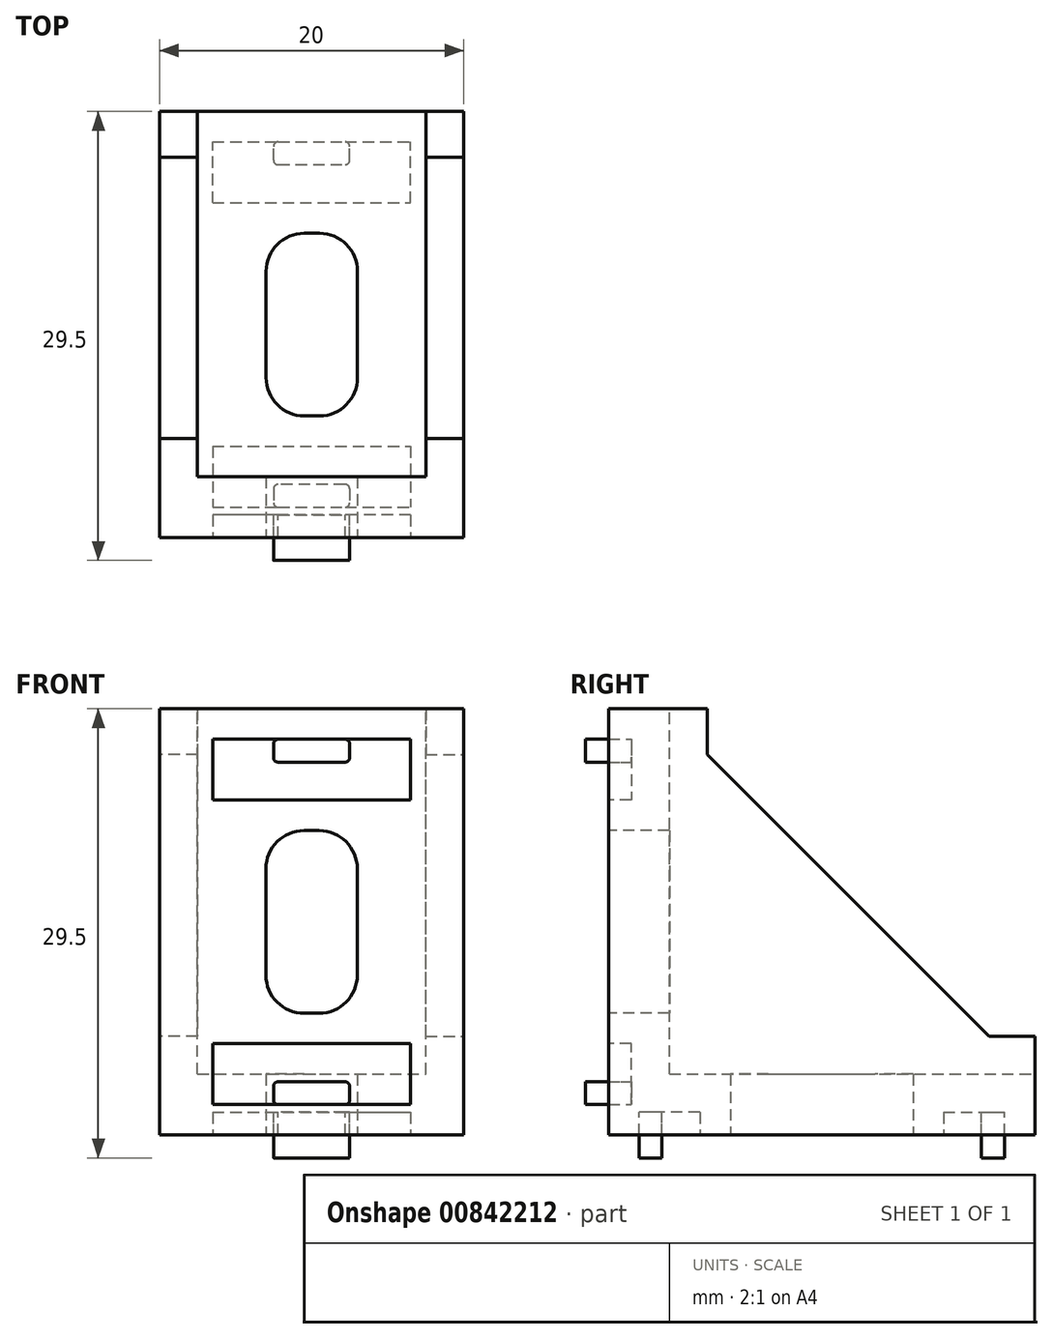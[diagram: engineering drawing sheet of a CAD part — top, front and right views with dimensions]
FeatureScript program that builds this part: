
annotation { "Feature Type Name" : "Feature", "Feature Type Description" : "" }
export const myFeature = defineFeature(function(context is Context, id is Id, definition is map)
    precondition{}
    {
        {
            var Q0;
            Q0=qCreatedBy(makeId("Top.planeOp"),FACE);
            var sketch = newSketch(context, id + "F0", { "sketchPlane" : qUnion([Q0])});
            skLineSegment(sketch, "E0.bottom", {"start": v(0, 0) * mm, "end": v(-20, 0) * mm});
            skLineSegment(sketch, "E0.top", {"start": v(0, 28) * mm, "end": v(-20, 28) * mm});
            skLineSegment(sketch, "E0.left", {"start": v(0, 0) * mm, "end": v(0, 28) * mm});
            skLineSegment(sketch, "E0.right", {"start": v(-20, 0) * mm, "end": v(-20, 28) * mm});
            skSolve(sketch);
        }
        {
            var Q0;
            Q0=makeQuery(id+"F0.imprint","IMPRINT",FACE,{"disambiguationData":[TD([[makeQuery(id+"F0.imprint","IMPRINT",EDGE,{"derivedFrom":sQuery(id+"F0.wireOp",EDGE,"E0.bottom")}),-1.0]])]});
            extrude(context, id + "F1", {"entities" : qUnion([Q0]), "depth" : 4 * mm, "offsetDistance" : 25 * mm});
        }
        {
            var Q0;
            Q0=qCreatedBy(makeId("Front.planeOp"),FACE);
            var sketch = newSketch(context, id + "F2", { "sketchPlane" : qUnion([Q0])});
            skLineSegment(sketch, "E1.bottom", {"start": v(0, 0) * mm, "end": v(-20, 0) * mm});
            skLineSegment(sketch, "E1.top", {"start": v(0, 28) * mm, "end": v(-20, 28) * mm});
            skLineSegment(sketch, "E1.left", {"start": v(0, 0) * mm, "end": v(0, 28) * mm});
            skLineSegment(sketch, "E1.right", {"start": v(-20, 0) * mm, "end": v(-20, 28) * mm});
            skSolve(sketch);
        }
        {
            var Q0;
            Q0=makeQuery(id+"F2.imprint","IMPRINT",FACE,{"disambiguationData":[TD([[makeQuery(id+"F2.imprint","IMPRINT",EDGE,{"derivedFrom":sQuery(id+"F2.wireOp",EDGE,"E1.bottom")}),-1.0]])]});
            extrude(context, id + "F3", {"entities" : qUnion([Q0]), "operationType" : NewBodyOperationType.ADD, "oppositeDirection" : true, "depth" : 4 * mm, "offsetDistance" : 25 * mm});
        }
        {
            var Q0;
            Q0=makeQuery(id+"F3.boolean.opBoolean","MERGE",FACE,{"derivedFrom":[makeQuery(id+"F1.opExtrude","SWEPT_FACE",FACE,{"disambiguationData":[OSD([sQuery(id+"F0.wireOp",EDGE,"E0.bottom")])]}),makeQuery(id+"F3.opExtrude","CAP_FACE",FACE,{"disambiguationData":[OSD([sQuery(id+"F2.wireOp",EDGE,"E1.bottom"),sQuery(id+"F2.wireOp",EDGE,"E1.top"),sQuery(id+"F2.wireOp",EDGE,"E1.left"),sQuery(id+"F2.wireOp",EDGE,"E1.right")])],"isStart":true})]});
            var sketch = newSketch(context, id + "F4", { "sketchPlane" : qUnion([Q0])});
            skLineSegment(sketch, "E2.bottom", {"start": v(-3.5, 2) * mm, "end": v(-16.5, 2) * mm});
            skLineSegment(sketch, "E2.top", {"start": v(-3.5, 6) * mm, "end": v(-16.5, 6) * mm});
            skLineSegment(sketch, "E2.left", {"start": v(-3.5, 2) * mm, "end": v(-3.5, 6) * mm});
            skLineSegment(sketch, "E2.right", {"start": v(-16.5, 2) * mm, "end": v(-16.5, 6) * mm});
            skLineSegment(sketch, "E3.MirrorCS", {"start": v(-16.5, 26) * mm, "end": v(-16.5, 22) * mm});
            skLineSegment(sketch, "E4.MirrorCS", {"start": v(-3.5, 26) * mm, "end": v(-3.5, 22) * mm});
            skLineSegment(sketch, "E5.MirrorCS", {"start": v(-3.5, 22) * mm, "end": v(-16.5, 22) * mm});
            skLineSegment(sketch, "E6.MirrorCS", {"start": v(-3.5, 26) * mm, "end": v(-16.5, 26) * mm});
            skSolve(sketch);
        }
        {
            var Q0;
            Q0=makeQuery(id+"F4.imprint","IMPRINT",FACE,{"disambiguationData":[TD([[makeQuery(id+"F4.imprint","IMPRINT",EDGE,{"derivedFrom":sQuery(id+"F4.wireOp",EDGE,"E2.bottom")}),-1.0]])]});
            var Q1;
            Q1=makeQuery(id+"F4.imprint","IMPRINT",FACE,{"disambiguationData":[TD([[makeQuery(id+"F4.imprint","IMPRINT",EDGE,{"derivedFrom":sQuery(id+"F4.wireOp",EDGE,"E3.MirrorCS")}),1.0]])]});
            extrude(context, id + "F5", {"entities" : qUnion([Q0, Q1]), "operationType" : NewBodyOperationType.REMOVE, "oppositeDirection" : true, "depth" : 1.5 * mm, "offsetDistance" : 25 * mm});
        }
        {
            var Q0;
            Q0=makeQuery(id+"F5.boolean.opBoolean","COPY",FACE,{"derivedFrom":makeQuery(id+"F5.opExtrude","CAP_FACE",FACE,{"disambiguationData":[OSD([sQuery(id+"F4.wireOp",EDGE,"E2.bottom"),sQuery(id+"F4.wireOp",EDGE,"E2.top"),sQuery(id+"F4.wireOp",EDGE,"E2.left"),sQuery(id+"F4.wireOp",EDGE,"E2.right")])],"isStart":false})});
            var sketch = newSketch(context, id + "F6", { "sketchPlane" : qUnion([Q0])});
            skPoint(sketch, "E7", {"position": v(-10, 2) * mm});
            skLineSegment(sketch, "E8.bottom", {"start": v(-12.2, 3.5) * mm, "end": v(-7.8, 3.5) * mm});
            skLineSegment(sketch, "E8.top", {"start": v(-12.2, 2) * mm, "end": v(-7.8, 2) * mm});
            skLineSegment(sketch, "E8.left", {"start": v(-12.5, 3.2) * mm, "end": v(-12.5, 2.3) * mm});
            skLineSegment(sketch, "E8.right", {"start": v(-7.5, 3.2) * mm, "end": v(-7.5, 2.3) * mm});
            skPoint(sketch, "E8.middle", {"position": v(-10, 2.75) * mm});
            skPoint(sketch, "E9.visualSharp", {"position": v(-7.5, 2) * mm});
            skArc(sketch, "E9.filletArc", {"start": v(-7.8, 2) * mm, "mid": v(-7.59, 2.09) * mm, "end": v(-7.5, 2.3) * mm});
            skPoint(sketch, "E10.visualSharp", {"position": v(-7.5, 3.5) * mm});
            skArc(sketch, "E10.filletArc", {"start": v(-7.5, 3.2) * mm, "mid": v(-7.59, 3.41) * mm, "end": v(-7.8, 3.5) * mm});
            skPoint(sketch, "E11.visualSharp", {"position": v(-12.5, 3.5) * mm});
            skArc(sketch, "E11.filletArc", {"start": v(-12.2, 3.5) * mm, "mid": v(-12.41, 3.41) * mm, "end": v(-12.5, 3.2) * mm});
            skPoint(sketch, "E12.visualSharp", {"position": v(-12.5, 2) * mm});
            skArc(sketch, "E12.filletArc", {"start": v(-12.5, 2.3) * mm, "mid": v(-12.41, 2.09) * mm, "end": v(-12.2, 2) * mm});
            skSolve(sketch);
        }
        {
            var Q0;
            Q0=makeQuery(id+"F6.imprint","IMPRINT",FACE,{"disambiguationData":[TD([[makeQuery(id+"F6.imprint","IMPRINT",EDGE,{"derivedFrom":sQuery(id+"F6.wireOp",EDGE,"E8.bottom")}),-1.0]])]});
            extrude(context, id + "F7", {"entities" : qUnion([Q0]), "operationType" : NewBodyOperationType.ADD, "depth" : 3 * mm, "offsetDistance" : 25 * mm});
        }
        {
            var Q0;
            Q0=makeQuery(id+"F5.boolean.opBoolean","COPY",FACE,{"derivedFrom":makeQuery(id+"F5.opExtrude","CAP_FACE",FACE,{"disambiguationData":[OSD([sQuery(id+"F4.wireOp",EDGE,"E3.MirrorCS"),sQuery(id+"F4.wireOp",EDGE,"E4.MirrorCS"),sQuery(id+"F4.wireOp",EDGE,"E5.MirrorCS"),sQuery(id+"F4.wireOp",EDGE,"E6.MirrorCS")])],"isStart":false})});
            var sketch = newSketch(context, id + "F8", { "sketchPlane" : qUnion([Q0])});
            skPoint(sketch, "E13", {"position": v(-10, 26) * mm});
            skLineSegment(sketch, "E14.bottom", {"start": v(-12.2, 26) * mm, "end": v(-7.8, 26) * mm});
            skLineSegment(sketch, "E14.top", {"start": v(-12.2, 24.5) * mm, "end": v(-7.8, 24.5) * mm});
            skLineSegment(sketch, "E14.left", {"start": v(-12.5, 25.7) * mm, "end": v(-12.5, 24.8) * mm});
            skLineSegment(sketch, "E14.right", {"start": v(-7.5, 25.7) * mm, "end": v(-7.5, 24.8) * mm});
            skPoint(sketch, "E14.middle", {"position": v(-10, 25.25) * mm});
            skPoint(sketch, "E15.visualSharp", {"position": v(-7.5, 24.5) * mm});
            skArc(sketch, "E15.filletArc", {"start": v(-7.8, 24.5) * mm, "mid": v(-7.59, 24.59) * mm, "end": v(-7.5, 24.8) * mm});
            skPoint(sketch, "E16.visualSharp", {"position": v(-12.5, 24.5) * mm});
            skArc(sketch, "E16.filletArc", {"start": v(-12.5, 24.8) * mm, "mid": v(-12.41, 24.59) * mm, "end": v(-12.2, 24.5) * mm});
            skPoint(sketch, "E17.visualSharp", {"position": v(-7.5, 26) * mm});
            skArc(sketch, "E17.filletArc", {"start": v(-7.5, 25.7) * mm, "mid": v(-7.59, 25.91) * mm, "end": v(-7.8, 26) * mm});
            skPoint(sketch, "E18.visualSharp", {"position": v(-12.5, 26) * mm});
            skArc(sketch, "E18.filletArc", {"start": v(-12.2, 26) * mm, "mid": v(-12.41, 25.91) * mm, "end": v(-12.5, 25.7) * mm});
            skSolve(sketch);
        }
        {
            var Q0;
            Q0=makeQuery(id+"F8.imprint","IMPRINT",FACE,{"disambiguationData":[TD([[makeQuery(id+"F8.imprint","IMPRINT",EDGE,{"derivedFrom":sQuery(id+"F8.wireOp",EDGE,"E14.bottom")}),1.0]])]});
            extrude(context, id + "F9", {"entities" : qUnion([Q0]), "operationType" : NewBodyOperationType.ADD, "depth" : 3 * mm, "offsetDistance" : 25 * mm});
        }
        {
            var Q0;
            Q0=makeQuery(id+"F3.boolean.opBoolean","MERGE",FACE,{"derivedFrom":[makeQuery(id+"F1.opExtrude","SWEPT_FACE",FACE,{"disambiguationData":[OSD([sQuery(id+"F0.wireOp",EDGE,"E0.bottom")])]}),makeQuery(id+"F3.opExtrude","CAP_FACE",FACE,{"disambiguationData":[OSD([sQuery(id+"F2.wireOp",EDGE,"E1.bottom"),sQuery(id+"F2.wireOp",EDGE,"E1.top"),sQuery(id+"F2.wireOp",EDGE,"E1.left"),sQuery(id+"F2.wireOp",EDGE,"E1.right")])],"isStart":true})]});
            var sketch = newSketch(context, id + "F10", { "sketchPlane" : qUnion([Q0])});
            skLineSegment(sketch, "E19", {"start": v(0, 14) * mm, "end": v(-20, 14) * mm});
            skLineSegment(sketch, "E20.bottom", {"start": v(-10.5, 20) * mm, "end": v(-9.5, 20) * mm});
            skLineSegment(sketch, "E20.top", {"start": v(-10.5, 8) * mm, "end": v(-9.5, 8) * mm});
            skLineSegment(sketch, "E20.left", {"start": v(-13, 17.5) * mm, "end": v(-13, 10.5) * mm});
            skLineSegment(sketch, "E20.right", {"start": v(-7, 17.5) * mm, "end": v(-7, 10.5) * mm});
            skPoint(sketch, "E20.middle", {"position": v(-10, 14) * mm});
            skPoint(sketch, "E21.visualSharp", {"position": v(-7, 8) * mm});
            skArc(sketch, "E21.filletArc", {"start": v(-9.5, 8) * mm, "mid": v(-7.73, 8.73) * mm, "end": v(-7, 10.5) * mm});
            skPoint(sketch, "E22.visualSharp", {"position": v(-13, 8) * mm});
            skArc(sketch, "E22.filletArc", {"start": v(-13, 10.5) * mm, "mid": v(-12.27, 8.73) * mm, "end": v(-10.5, 8) * mm});
            skPoint(sketch, "E23.visualSharp", {"position": v(-7, 20) * mm});
            skArc(sketch, "E23.filletArc", {"start": v(-7, 17.5) * mm, "mid": v(-7.73, 19.27) * mm, "end": v(-9.5, 20) * mm});
            skPoint(sketch, "E24.visualSharp", {"position": v(-13, 20) * mm});
            skArc(sketch, "E24.filletArc", {"start": v(-10.5, 20) * mm, "mid": v(-12.27, 19.27) * mm, "end": v(-13, 17.5) * mm});
            skSolve(sketch);
        }
        {
            var Q0;
            Q0 = qSketchRegion(id + "F10", true);
            extrude(context, id + "F11", {"entities" : qUnion([Q0]), "operationType" : NewBodyOperationType.REMOVE, "oppositeDirection" : true, "depth" : 4 * mm, "offsetDistance" : 25 * mm});
        }
        {
            var Q0;
            Q0=makeQuery(id+"F1.opExtrude","CAP_FACE",FACE,{"disambiguationData":[OSD([sQuery(id+"F0.wireOp",EDGE,"E0.bottom"),sQuery(id+"F0.wireOp",EDGE,"E0.top"),sQuery(id+"F0.wireOp",EDGE,"E0.left"),sQuery(id+"F0.wireOp",EDGE,"E0.right")])],"isStart":true});
            var sketch = newSketch(context, id + "F12", { "sketchPlane" : qUnion([Q0])});
            skLineSegment(sketch, "E25.bottom", {"start": v(-16.5, -22) * mm, "end": v(-3.5, -22) * mm});
            skLineSegment(sketch, "E25.top", {"start": v(-16.5, -26) * mm, "end": v(-3.5, -26) * mm});
            skLineSegment(sketch, "E25.left", {"start": v(-16.5, -22) * mm, "end": v(-16.5, -26) * mm});
            skLineSegment(sketch, "E25.right", {"start": v(-3.5, -22) * mm, "end": v(-3.5, -26) * mm});
            skPoint(sketch, "E25.middle", {"position": v(-10, -24) * mm});
            skLineSegment(sketch, "E26", {"start": v(0, -14) * mm, "end": v(-4.91, -14) * mm});
            skLineSegment(sketch, "E27.MirrorCS", {"start": v(-16.5, -6) * mm, "end": v(-3.5, -6) * mm});
            skLineSegment(sketch, "E28.MirrorCS", {"start": v(-3.5, -6) * mm, "end": v(-3.5, -2) * mm});
            skLineSegment(sketch, "E29.MirrorCS", {"start": v(-16.5, -2) * mm, "end": v(-3.5, -2) * mm});
            skLineSegment(sketch, "E30.MirrorCS", {"start": v(-16.5, -6) * mm, "end": v(-16.5, -2) * mm});
            skPoint(sketch, "E31.MirrorP", {"position": v(-10, -4) * mm});
            skSolve(sketch);
        }
        {
            var Q0;
            Q0=makeQuery(id+"F12.imprint","IMPRINT",FACE,{"disambiguationData":[TD([[makeQuery(id+"F12.imprint","IMPRINT",EDGE,{"derivedFrom":sQuery(id+"F12.wireOp",EDGE,"E25.bottom")}),-1.0]])]});
            var Q1;
            Q1=makeQuery(id+"F12.imprint","IMPRINT",FACE,{"disambiguationData":[TD([[makeQuery(id+"F12.imprint","IMPRINT",EDGE,{"derivedFrom":sQuery(id+"F12.wireOp",EDGE,"E27.MirrorCS")}),1.0]])]});
            extrude(context, id + "F13", {"entities" : qUnion([Q0, Q1]), "operationType" : NewBodyOperationType.REMOVE, "oppositeDirection" : true, "depth" : 1.5 * mm, "offsetDistance" : 25 * mm});
        }
        {
            var Q0;
            Q0=makeQuery(id+"F1.opExtrude","CAP_FACE",FACE,{"disambiguationData":[OSD([sQuery(id+"F0.wireOp",EDGE,"E0.bottom"),sQuery(id+"F0.wireOp",EDGE,"E0.top"),sQuery(id+"F0.wireOp",EDGE,"E0.left"),sQuery(id+"F0.wireOp",EDGE,"E0.right")])],"isStart":true});
            var sketch = newSketch(context, id + "F14", { "sketchPlane" : qUnion([Q0])});
            skLineSegment(sketch, "E32.bottom", {"start": v(-10.48, -8) * mm, "end": v(-9.48, -8) * mm});
            skLineSegment(sketch, "E32.top", {"start": v(-10.48, -20) * mm, "end": v(-9.48, -20) * mm});
            skLineSegment(sketch, "E32.left", {"start": v(-12.98, -10.5) * mm, "end": v(-12.98, -17.5) * mm});
            skLineSegment(sketch, "E32.right", {"start": v(-6.98, -10.5) * mm, "end": v(-6.98, -17.5) * mm});
            skPoint(sketch, "E32.middle", {"position": v(-9.98, -14) * mm});
            skLineSegment(sketch, "E33", {"start": v(0, -14) * mm, "end": v(-20, -14) * mm});
            skPoint(sketch, "E34.visualSharp", {"position": v(-6.98, -20) * mm});
            skArc(sketch, "E34.filletArc", {"start": v(-9.48, -20) * mm, "mid": v(-7.72, -19.27) * mm, "end": v(-6.98, -17.5) * mm});
            skPoint(sketch, "E35.visualSharp", {"position": v(-12.98, -20) * mm});
            skArc(sketch, "E35.filletArc", {"start": v(-12.98, -17.5) * mm, "mid": v(-12.25, -19.27) * mm, "end": v(-10.48, -20) * mm});
            skPoint(sketch, "E36.visualSharp", {"position": v(-12.98, -8) * mm});
            skArc(sketch, "E36.filletArc", {"start": v(-10.48, -8) * mm, "mid": v(-12.25, -8.73) * mm, "end": v(-12.98, -10.5) * mm});
            skPoint(sketch, "E37.visualSharp", {"position": v(-6.98, -8) * mm});
            skArc(sketch, "E37.filletArc", {"start": v(-6.98, -10.5) * mm, "mid": v(-7.72, -8.73) * mm, "end": v(-9.48, -8) * mm});
            skSolve(sketch);
        }
        {
            var Q0;
            Q0=makeQuery(id+"F14.imprint","IMPRINT",FACE,{"disambiguationData":[TD([[makeQuery(id+"F14.imprint","IMPRINT",EDGE,{"derivedFrom":sQuery(id+"F14.wireOp",EDGE,"E32.top")}),1.0]])]});
            var Q1;
            Q1=makeQuery(id+"F14.imprint","IMPRINT",FACE,{"disambiguationData":[TD([[makeQuery(id+"F14.imprint","IMPRINT",EDGE,{"derivedFrom":sQuery(id+"F14.wireOp",EDGE,"E32.bottom")}),-1.0]])]});
            extrude(context, id + "F15", {"entities" : qUnion([Q0, Q1]), "operationType" : NewBodyOperationType.REMOVE, "oppositeDirection" : true, "depth" : 4 * mm, "offsetDistance" : 25 * mm});
        }
        {
            var Q0;
            Q0=makeQuery(id+"F13.boolean.opBoolean","COPY",FACE,{"derivedFrom":makeQuery(id+"F13.opExtrude","CAP_FACE",FACE,{"disambiguationData":[OSD([sQuery(id+"F12.wireOp",EDGE,"E25.bottom"),sQuery(id+"F12.wireOp",EDGE,"E25.top"),sQuery(id+"F12.wireOp",EDGE,"E25.left"),sQuery(id+"F12.wireOp",EDGE,"E25.right")])],"isStart":false})});
            var sketch = newSketch(context, id + "F16", { "sketchPlane" : qUnion([Q0])});
            skPoint(sketch, "E38", {"position": v(-10, -26) * mm});
            skLineSegment(sketch, "E39.bottom", {"start": v(-12.2, -24.5) * mm, "end": v(-7.8, -24.5) * mm});
            skLineSegment(sketch, "E39.top", {"start": v(-12.2, -26) * mm, "end": v(-7.8, -26) * mm});
            skLineSegment(sketch, "E39.left", {"start": v(-12.5, -24.8) * mm, "end": v(-12.5, -25.7) * mm});
            skLineSegment(sketch, "E39.right", {"start": v(-7.5, -24.8) * mm, "end": v(-7.5, -25.7) * mm});
            skPoint(sketch, "E39.middle", {"position": v(-10, -25.25) * mm});
            skPoint(sketch, "E40.visualSharp", {"position": v(-7.5, -26) * mm});
            skArc(sketch, "E40.filletArc", {"start": v(-7.8, -26) * mm, "mid": v(-7.59, -25.91) * mm, "end": v(-7.5, -25.7) * mm});
            skPoint(sketch, "E41.visualSharp", {"position": v(-7.5, -24.5) * mm});
            skArc(sketch, "E41.filletArc", {"start": v(-7.5, -24.8) * mm, "mid": v(-7.59, -24.59) * mm, "end": v(-7.8, -24.5) * mm});
            skPoint(sketch, "E42.visualSharp", {"position": v(-12.5, -24.5) * mm});
            skArc(sketch, "E42.filletArc", {"start": v(-12.2, -24.5) * mm, "mid": v(-12.41, -24.59) * mm, "end": v(-12.5, -24.8) * mm});
            skPoint(sketch, "E43.visualSharp", {"position": v(-12.5, -26) * mm});
            skArc(sketch, "E43.filletArc", {"start": v(-12.5, -25.7) * mm, "mid": v(-12.41, -25.91) * mm, "end": v(-12.2, -26) * mm});
            skSolve(sketch);
        }
        {
            var Q0;
            Q0=makeQuery(id+"F16.imprint","IMPRINT",FACE,{"disambiguationData":[TD([[makeQuery(id+"F16.imprint","IMPRINT",EDGE,{"derivedFrom":sQuery(id+"F16.wireOp",EDGE,"E39.bottom")}),-1.0]])]});
            extrude(context, id + "F17", {"entities" : qUnion([Q0]), "operationType" : NewBodyOperationType.ADD, "depth" : 3 * mm, "offsetDistance" : 25 * mm});
        }
        {
            var Q0;
            Q0=makeQuery(id+"F13.boolean.opBoolean","COPY",FACE,{"derivedFrom":makeQuery(id+"F13.opExtrude","CAP_FACE",FACE,{"disambiguationData":[OSD([sQuery(id+"F12.wireOp",EDGE,"E27.MirrorCS"),sQuery(id+"F12.wireOp",EDGE,"E28.MirrorCS"),sQuery(id+"F12.wireOp",EDGE,"E29.MirrorCS"),sQuery(id+"F12.wireOp",EDGE,"E30.MirrorCS")])],"isStart":false})});
            var sketch = newSketch(context, id + "F18", { "sketchPlane" : qUnion([Q0])});
            skPoint(sketch, "E44", {"position": v(-10, -2) * mm});
            skLineSegment(sketch, "E45.bottom", {"start": v(-7.8, -3.5) * mm, "end": v(-12.2, -3.5) * mm});
            skLineSegment(sketch, "E45.top", {"start": v(-7.8, -2) * mm, "end": v(-12.2, -2) * mm});
            skLineSegment(sketch, "E45.left", {"start": v(-7.5, -3.2) * mm, "end": v(-7.5, -2.3) * mm});
            skLineSegment(sketch, "E45.right", {"start": v(-12.5, -3.2) * mm, "end": v(-12.5, -2.3) * mm});
            skPoint(sketch, "E45.middle", {"position": v(-10, -2.75) * mm});
            skPoint(sketch, "E46.visualSharp", {"position": v(-12.5, -2) * mm});
            skArc(sketch, "E46.filletArc", {"start": v(-12.2, -2) * mm, "mid": v(-12.41, -2.09) * mm, "end": v(-12.5, -2.3) * mm});
            skPoint(sketch, "E47.visualSharp", {"position": v(-12.5, -3.5) * mm});
            skArc(sketch, "E47.filletArc", {"start": v(-12.5, -3.2) * mm, "mid": v(-12.41, -3.41) * mm, "end": v(-12.2, -3.5) * mm});
            skPoint(sketch, "E48.visualSharp", {"position": v(-7.5, -3.5) * mm});
            skArc(sketch, "E48.filletArc", {"start": v(-7.8, -3.5) * mm, "mid": v(-7.59, -3.41) * mm, "end": v(-7.5, -3.2) * mm});
            skPoint(sketch, "E49.visualSharp", {"position": v(-7.5, -2) * mm});
            skArc(sketch, "E49.filletArc", {"start": v(-7.5, -2.3) * mm, "mid": v(-7.59, -2.09) * mm, "end": v(-7.8, -2) * mm});
            skSolve(sketch);
        }
        {
            var Q0;
            Q0=makeQuery(id+"F18.imprint","IMPRINT",FACE,{"disambiguationData":[TD([[makeQuery(id+"F18.imprint","IMPRINT",EDGE,{"derivedFrom":sQuery(id+"F18.wireOp",EDGE,"E45.bottom")}),-1.0]])]});
            extrude(context, id + "F19", {"entities" : qUnion([Q0]), "operationType" : NewBodyOperationType.ADD, "depth" : 3 * mm, "offsetDistance" : 25 * mm});
        }
        {
            var Q0;
            Q0=makeQuery(id+"F3.boolean.opBoolean","MERGE",FACE,{"derivedFrom":[makeQuery(id+"F1.opExtrude","SWEPT_FACE",FACE,{"disambiguationData":[OSD([sQuery(id+"F0.wireOp",EDGE,"E0.left")])]}),makeQuery(id+"F3.opExtrude","SWEPT_FACE",FACE,{"disambiguationData":[OSD([sQuery(id+"F2.wireOp",EDGE,"E1.left")])]})]});
            var sketch = newSketch(context, id + "F20", { "sketchPlane" : qUnion([Q0])});
            skLineSegment(sketch, "E50", {"start": v(28, 4) * mm, "end": v(4, 4) * mm});
            skLineSegment(sketch, "E51", {"start": v(4, 4) * mm, "end": v(4, 28) * mm});
            skLineSegment(sketch, "E52", {"start": v(4, 28) * mm, "end": v(6.5, 28) * mm});
            skLineSegment(sketch, "E53", {"start": v(6.5, 28) * mm, "end": v(6.5, 25) * mm});
            skLineSegment(sketch, "E54", {"start": v(28, 4) * mm, "end": v(28, 6.5) * mm});
            skLineSegment(sketch, "E55", {"start": v(28, 6.5) * mm, "end": v(25, 6.5) * mm});
            skLineSegment(sketch, "E56", {"start": v(25, 6.5) * mm, "end": v(6.5, 25) * mm});
            skSolve(sketch);
        }
        {
            var Q0;
            Q0=makeQuery(id+"F20.imprint","IMPRINT",FACE,{"disambiguationData":[TD([[makeQuery(id+"F20.imprint","IMPRINT",EDGE,{"derivedFrom":sQuery(id+"F20.wireOp",EDGE,"E50")}),1.0]])]});
            extrude(context, id + "F21", {"entities" : qUnion([Q0]), "operationType" : NewBodyOperationType.ADD, "oppositeDirection" : true, "depth" : 2.5 * mm, "offsetDistance" : 25 * mm});
        }
        {
            var Q0;
            Q0=makeQuery(id+"F3.boolean.opBoolean","MERGE",FACE,{"derivedFrom":[makeQuery(id+"F1.opExtrude","SWEPT_FACE",FACE,{"disambiguationData":[OSD([sQuery(id+"F0.wireOp",EDGE,"E0.right")])]}),makeQuery(id+"F3.opExtrude","SWEPT_FACE",FACE,{"disambiguationData":[OSD([sQuery(id+"F2.wireOp",EDGE,"E1.right")])]})]});
            var sketch = newSketch(context, id + "F22", { "sketchPlane" : qUnion([Q0])});
            skLineSegment(sketch, "E57", {"start": v(-4, 28) * mm, "end": v(-4, 4) * mm});
            skLineSegment(sketch, "E58", {"start": v(-4, 4) * mm, "end": v(-28, 4) * mm});
            skLineSegment(sketch, "E59", {"start": v(-28, 4) * mm, "end": v(-28, 6.5) * mm});
            skLineSegment(sketch, "E60", {"start": v(-28, 6.5) * mm, "end": v(-25, 6.5) * mm});
            skLineSegment(sketch, "E61", {"start": v(-4, 28) * mm, "end": v(-6.5, 28) * mm});
            skLineSegment(sketch, "E62", {"start": v(-6.5, 28) * mm, "end": v(-6.5, 25) * mm});
            skLineSegment(sketch, "E63", {"start": v(-6.5, 25) * mm, "end": v(-25, 6.5) * mm});
            skSolve(sketch);
        }
        {
            var Q0;
            Q0=makeQuery(id+"F22.imprint","IMPRINT",FACE,{"disambiguationData":[TD([[makeQuery(id+"F22.imprint","IMPRINT",EDGE,{"derivedFrom":sQuery(id+"F22.wireOp",EDGE,"E57")}),1.0]])]});
            extrude(context, id + "F23", {"entities" : qUnion([Q0]), "operationType" : NewBodyOperationType.ADD, "oppositeDirection" : true, "depth" : 2.5 * mm, "offsetDistance" : 25 * mm});
        }
    });
